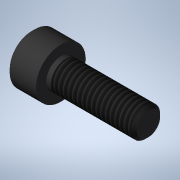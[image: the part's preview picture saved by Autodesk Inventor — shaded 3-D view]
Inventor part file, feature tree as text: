
AUTODESK INVENTOR PART (.ipt)
format: ipt  version: 2021 (Build 250183000, 183)  size: 151,040 bytes
history: native  units: mm
features: other x14, sketch x3, revolve x1, thread x1, hole x1, extrude x1
ambient origin geometry x8: Origin, YZ Plane, XZ Plane, XY Plane, X Axis, Y Axis, Z Axis, Center Point
bodies: Solid1 (feature_tree)
feature tree (21):
  revolve  "Revolution1"  [1 undecoded]
  thread  "Thread1"  [1 undecoded]
  hole  "Hole1"  [1 undecoded]
  extrude  "Extrusion1"  [1 undecoded]
  other  "bolt_XY"
  other  "bolt_YZ"
  other  "bolt_ZX"
  other  "bolt_X"
  other  "bolt_Y"
  other  "bolt_Z"
  other  "bolt_Center"
  other  "nut_XY"
  other  "nut_YZ"
  other  "nut_ZX"
  other  "nut_X"
  other  "nut_Y"
  other  "nut_Z"
  other  "nut_Center"
  sketch  "Sketch_1"  dims[d0=360.0deg d1=13.7095mm d2=0.0mm]
  sketch  "Sketch2"  dims[d3=4.0mm d4=6.0mm d5=4.0mm d6=2.0mm d7=90.0deg d8=2.5mm d9=120.0deg d10=2.5mm d11=0.0mm]
  sketch  "Sketch_3"  dims[d12=0.0mm d13=0.0mm]
note: 4 required parameter values undecoded (feature->parameter linkage not recoverable at this tier; creation-order binding heuristic only, values carry confidence <= 0.55)